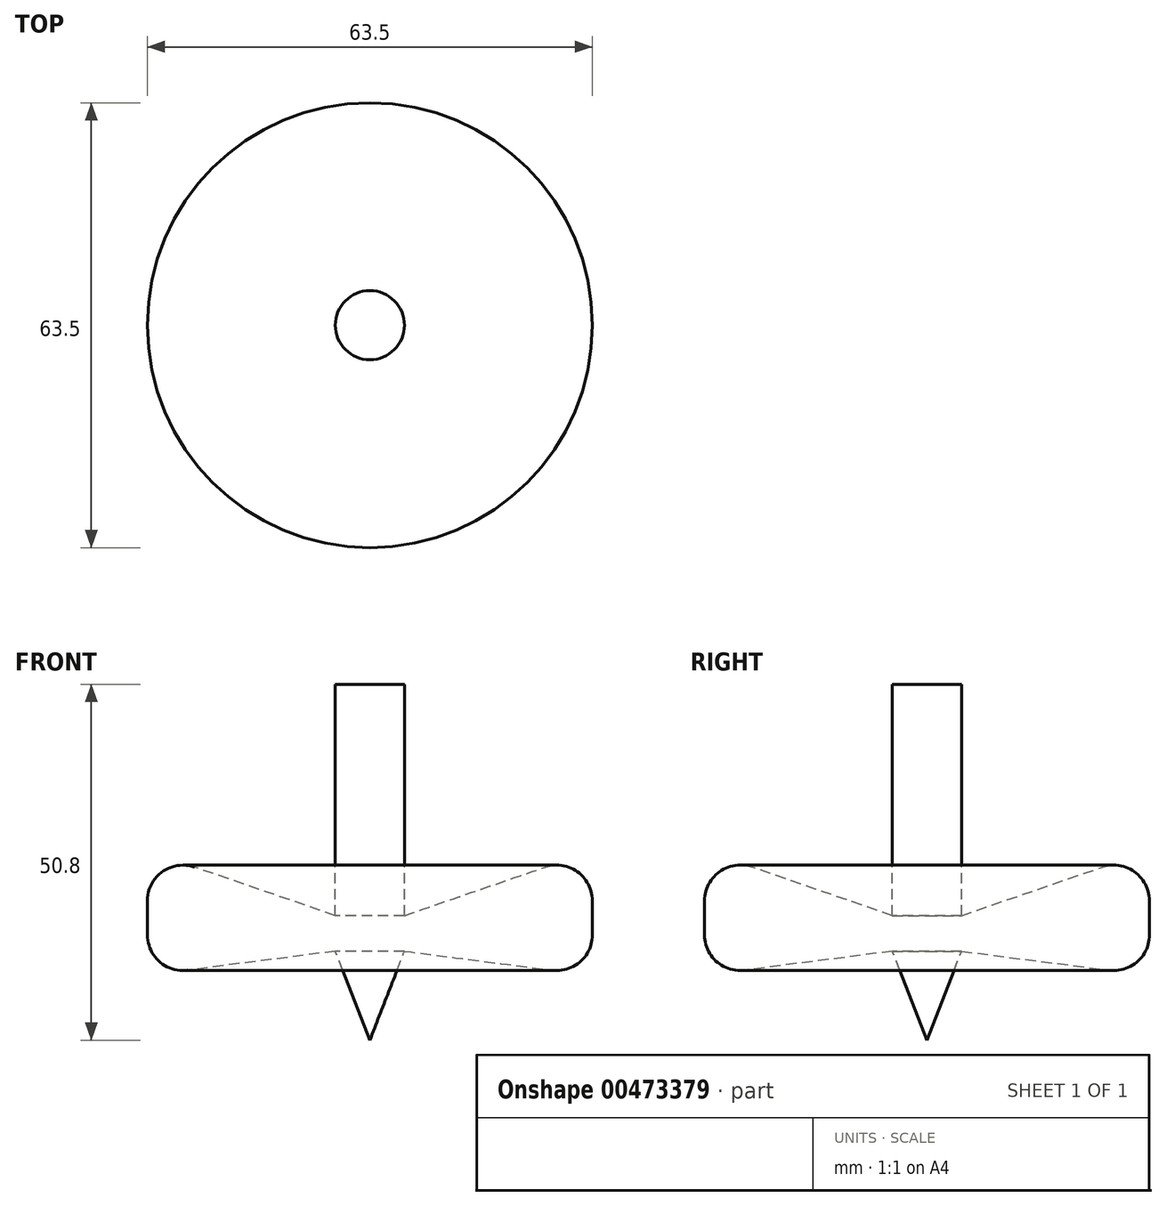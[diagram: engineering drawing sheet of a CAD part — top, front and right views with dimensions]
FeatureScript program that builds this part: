
annotation { "Feature Type Name" : "Feature", "Feature Type Description" : "" }
export const myFeature = defineFeature(function(context is Context, id is Id, definition is map)
    precondition{}
    {
        {
            var Q0;
            Q0=qCreatedBy(makeId("Front.planeOp"),FACE);
            var sketch = newSketch(context, id + "F0", { "sketchPlane" : qUnion([Q0])});
            skLineSegment(sketch, "E0", {"start": v(0, 0) * mm, "end": v(4.93, 12.7) * mm});
            skLineSegment(sketch, "E1", {"start": v(4.93, 12.7) * mm, "end": v(31.75, 9.24) * mm});
            skLineSegment(sketch, "E2", {"start": v(31.75, 9.24) * mm, "end": v(31.75, 27.02) * mm});
            skLineSegment(sketch, "E3", {"start": v(31.75, 27.02) * mm, "end": v(4.93, 17.78) * mm});
            skLineSegment(sketch, "E4", {"start": v(4.93, 17.78) * mm, "end": v(4.93, 50.8) * mm});
            skLineSegment(sketch, "E5", {"start": v(4.93, 50.8) * mm, "end": v(0, 50.8) * mm});
            skLineSegment(sketch, "E6", {"start": v(0, 50.8) * mm, "end": v(0, 0) * mm});
            skSolve(sketch);
        }
        {
            var Q0;
            Q0=makeQuery(id+"F0.imprint","IMPRINT",FACE,{"disambiguationData":[TD([[makeQuery(id+"F0.imprint","IMPRINT",EDGE,{"derivedFrom":sQuery(id+"F0.wireOp",EDGE,"E0")}),1.0]])]});
            var Q1;
            Q1=sQuery(id+"F0.wireOp",EDGE,"E6");
            revolve(context, id + "F1", {"entities" : qUnion([Q0]), "axis" : qUnion([Q1]), "revolveType" : RevolveType.FULL});
        }
        {
            var Q0;
            Q0=makeQuery(id+"F1.opRevolve","SWEPT_FACE",FACE,{"disambiguationData":[OSD([sQuery(id+"F0.wireOp",EDGE,"E2")])]});
            fillet(context, id + "F2", {"entities" : qUnion([Q0]), "radius" : 5.08 * mm, "tangentPropagation" : true, "allowEdgeOverflow" : false});
        }
    });
